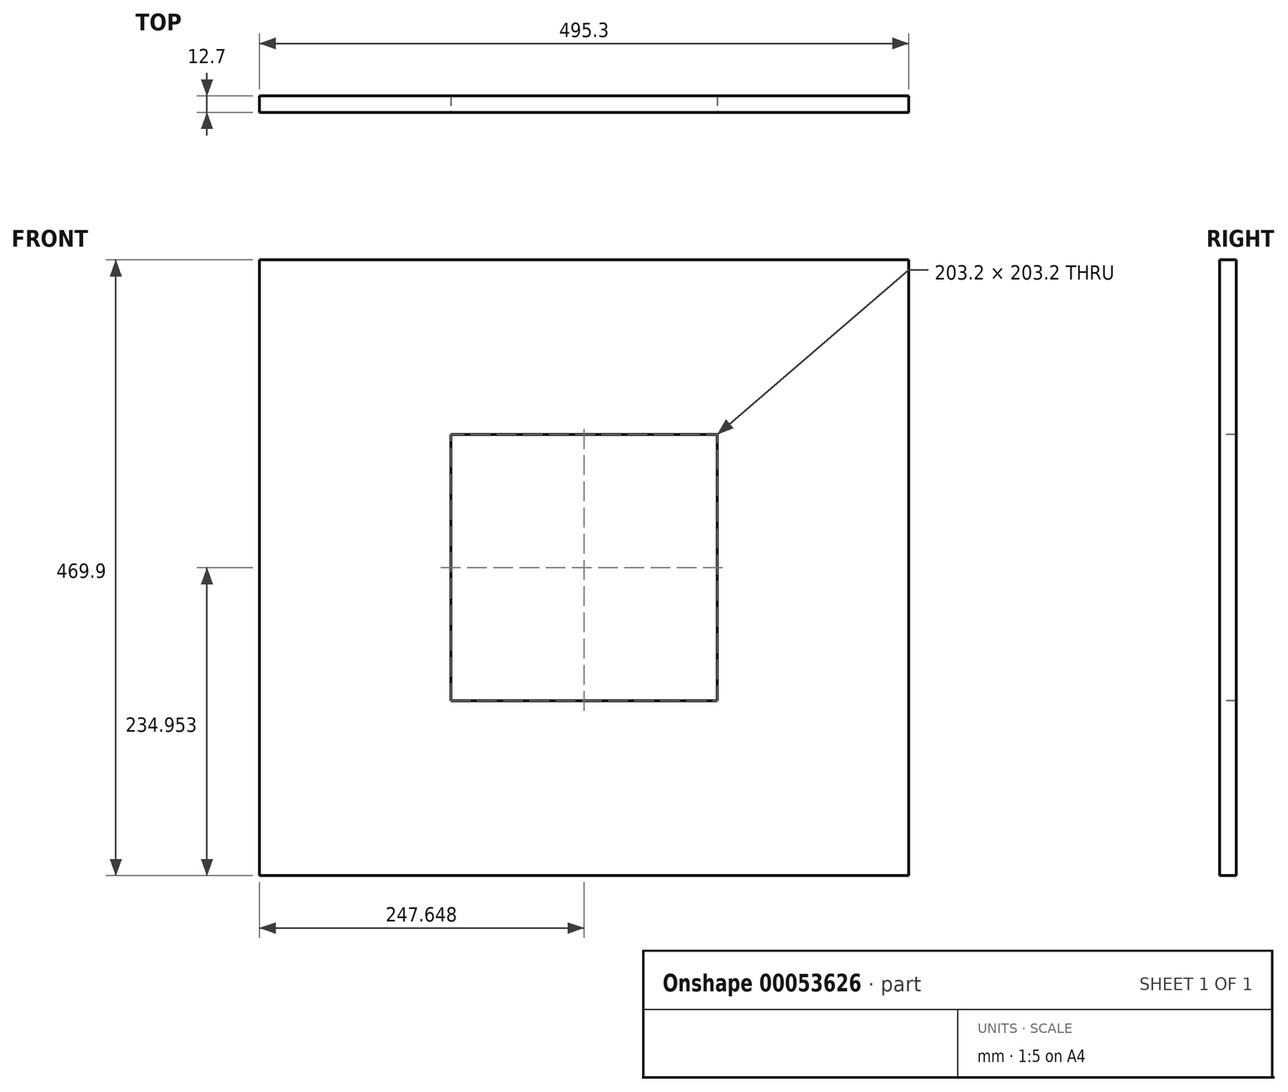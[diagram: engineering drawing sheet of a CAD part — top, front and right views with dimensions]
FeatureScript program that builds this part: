
annotation { "Feature Type Name" : "Feature", "Feature Type Description" : "" }
export const myFeature = defineFeature(function(context is Context, id is Id, definition is map)
    precondition{}
    {
        {
            var Q0;
            Q0=qCreatedBy(makeId("Front.planeOp"),FACE);
            var sketch = newSketch(context, id + "F0", { "sketchPlane" : qUnion([Q0])});
            skLineSegment(sketch, "E0.bottom", {"start": v(-244.7, 229.14) * mm, "end": v(250.6, 229.14) * mm});
            skLineSegment(sketch, "E0.top", {"start": v(-244.7, -240.76) * mm, "end": v(250.6, -240.76) * mm});
            skLineSegment(sketch, "E0.left", {"start": v(-244.7, 229.14) * mm, "end": v(-244.7, -240.76) * mm});
            skLineSegment(sketch, "E0.right", {"start": v(250.6, 229.14) * mm, "end": v(250.6, -240.76) * mm});
            skSolve(sketch);
        }
        {
            var Q0;
            Q0=makeQuery(id+"F0.imprint","IMPRINT",FACE,{"disambiguationData":[TD([[makeQuery(id+"F0.imprint","IMPRINT",EDGE,{"derivedFrom":sQuery(id+"F0.wireOp",EDGE,"E0.bottom")}),-1.0]])]});
            extrude(context, id + "F1", {"entities" : qUnion([Q0]), "depth" : 12.7 * mm});
        }
        {
            var Q0;
            Q0=makeQuery(id+"F1.opExtrude","CAP_FACE",FACE,{"disambiguationData":[OSD([sQuery(id+"F0.wireOp",EDGE,"E0.bottom"),sQuery(id+"F0.wireOp",EDGE,"E0.top"),sQuery(id+"F0.wireOp",EDGE,"E0.left"),sQuery(id+"F0.wireOp",EDGE,"E0.right")])],"isStart":false});
            var sketch = newSketch(context, id + "F2", { "sketchPlane" : qUnion([Q0])});
            skLineSegment(sketch, "E1.bottom", {"start": v(-98.65, 95.8) * mm, "end": v(104.55, 95.8) * mm});
            skLineSegment(sketch, "E1.top", {"start": v(-98.65, -107.4) * mm, "end": v(104.55, -107.4) * mm});
            skLineSegment(sketch, "E1.left", {"start": v(-98.65, 95.8) * mm, "end": v(-98.65, -107.4) * mm});
            skLineSegment(sketch, "E1.right", {"start": v(104.55, 95.8) * mm, "end": v(104.55, -107.4) * mm});
            skSolve(sketch);
        }
        {
            var Q0;
            Q0=makeQuery(id+"F2.imprint","IMPRINT",FACE,{"disambiguationData":[TD([[makeQuery(id+"F2.imprint","IMPRINT",EDGE,{"derivedFrom":sQuery(id+"F2.wireOp",EDGE,"E1.bottom")}),-1.0]])]});
            extrude(context, id + "F3", {"entities" : qUnion([Q0]), "operationType" : NewBodyOperationType.REMOVE, "endBound" : BoundingType.THROUGH_ALL, "oppositeDirection" : true, "depth" : 25.4 * mm});
        }
    });
